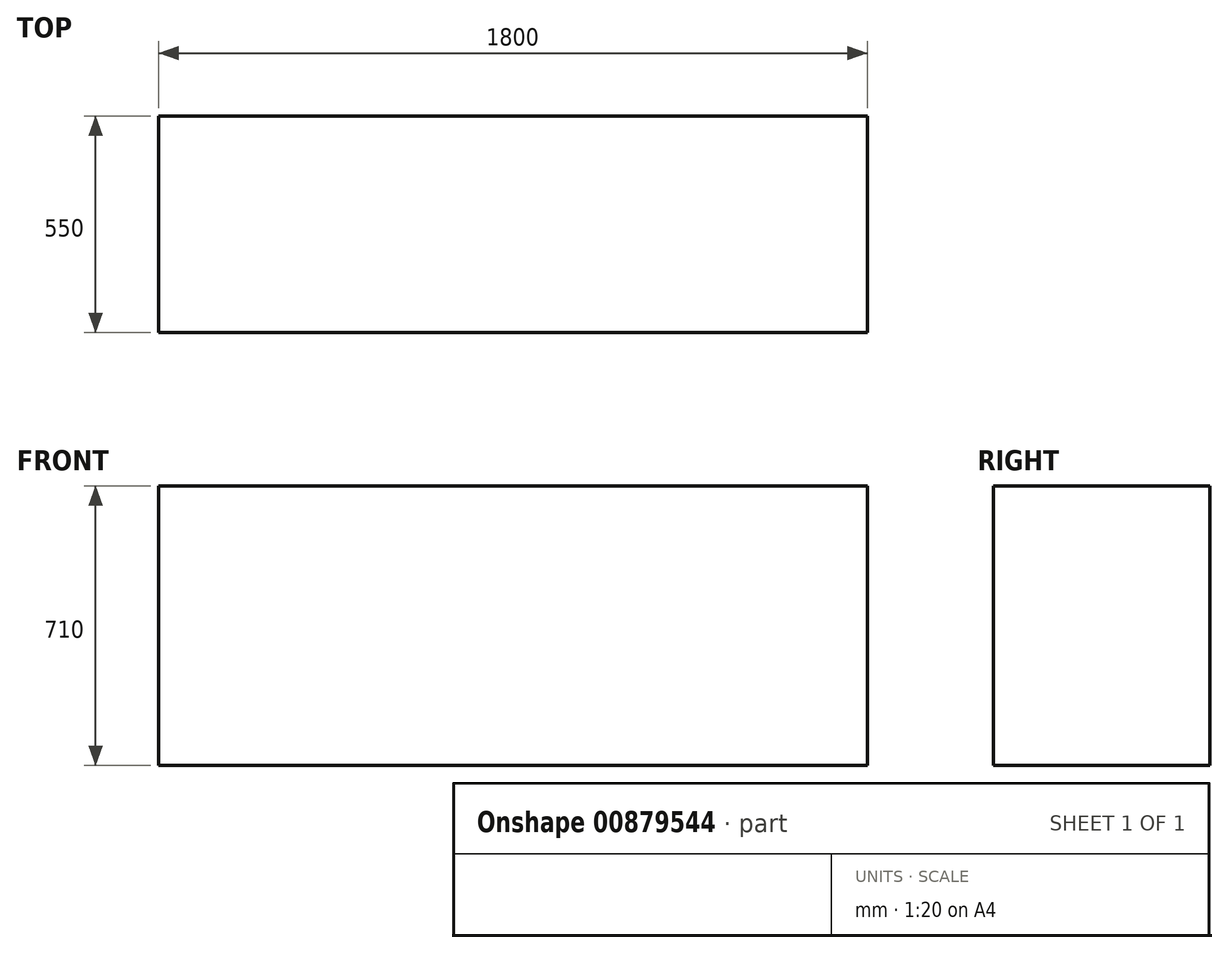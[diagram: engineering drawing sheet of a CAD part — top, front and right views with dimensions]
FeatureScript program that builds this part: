
annotation { "Feature Type Name" : "Feature", "Feature Type Description" : "" }
export const myFeature = defineFeature(function(context is Context, id is Id, definition is map)
    precondition{}
    {
        {
            var Q0;
            Q0=qCreatedBy(makeId("Front.planeOp"),FACE);
            var sketch = newSketch(context, id + "F0", { "sketchPlane" : qUnion([Q0])});
            skLineSegment(sketch, "E0.bottom", {"start": v(900, -355) * mm, "end": v(-900, -355) * mm});
            skLineSegment(sketch, "E0.top", {"start": v(900, 355) * mm, "end": v(-900, 355) * mm});
            skLineSegment(sketch, "E0.left", {"start": v(900, -355) * mm, "end": v(900, 355) * mm});
            skLineSegment(sketch, "E0.right", {"start": v(-900, -355) * mm, "end": v(-900, 355) * mm});
            skPoint(sketch, "E0.middle", {"position": v(0, 0) * mm});
            skSolve(sketch);
        }
        {
            var Q0;
            Q0 = qSketchRegion(id + "F0", true);
            extrude(context, id + "F1", {"entities" : qUnion([Q0]), "depth" : 550 * mm, "offsetDistance" : 25 * mm});
        }
    });
